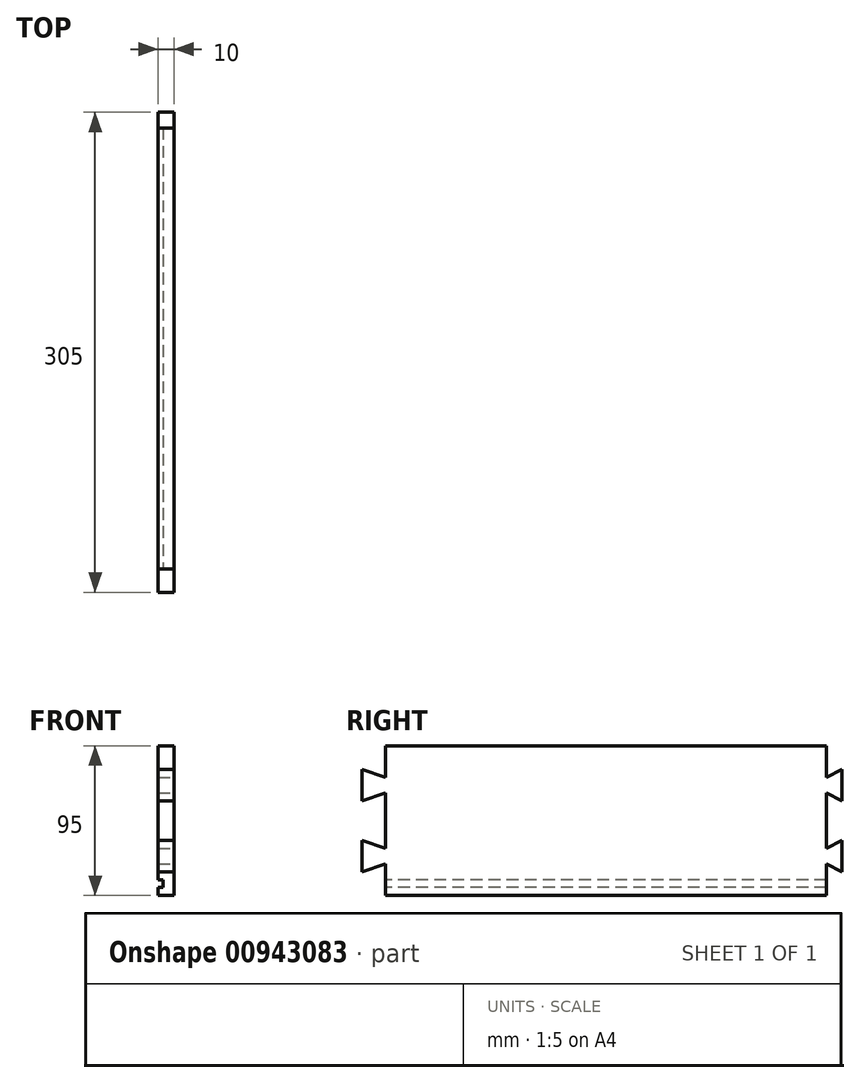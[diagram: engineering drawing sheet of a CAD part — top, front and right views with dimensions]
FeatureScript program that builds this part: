
annotation { "Feature Type Name" : "Feature", "Feature Type Description" : "" }
export const myFeature = defineFeature(function(context is Context, id is Id, definition is map)
    precondition{}
    {
        {
            var Q0;
            Q0=qCreatedBy(makeId("Right.planeOp"),FACE);
            var sketch = newSketch(context, id + "F0", { "sketchPlane" : qUnion([Q0])});
            skLineSegment(sketch, "E0.bottom", {"start": v(-82.46, 55.9) * mm, "end": v(222.54, 55.9) * mm});
            skLineSegment(sketch, "E0.top", {"start": v(-82.46, -39.1) * mm, "end": v(222.54, -39.1) * mm});
            skLineSegment(sketch, "E0.left", {"start": v(-82.46, 55.9) * mm, "end": v(-82.46, -39.1) * mm});
            skLineSegment(sketch, "E0.right", {"start": v(222.54, 55.9) * mm, "end": v(222.54, -39.1) * mm});
            skSolve(sketch);
        }
        {
            var Q0;
            Q0=makeQuery(id+"F0.imprint","IMPRINT",FACE,{"disambiguationData":[TD([[makeQuery(id+"F0.imprint","IMPRINT",EDGE,{"derivedFrom":sQuery(id+"F0.wireOp",EDGE,"E0.bottom")}),-1.0]])]});
            extrude(context, id + "F1", {"entities" : qUnion([Q0]), "depth" : 10 * mm, "offsetDistance" : 25 * mm});
        }
        {
            var Q0;
            Q0=makeQuery(id+"F1.opExtrude","CAP_FACE",FACE,{"disambiguationData":[OSD([sQuery(id+"F0.wireOp",EDGE,"E0.bottom"),sQuery(id+"F0.wireOp",EDGE,"E0.top"),sQuery(id+"F0.wireOp",EDGE,"E0.left"),sQuery(id+"F0.wireOp",EDGE,"E0.right")])],"isStart":false});
            var sketch = newSketch(context, id + "F2", { "sketchPlane" : qUnion([Q0])});
            skLineSegment(sketch, "E1", {"start": v(-82.46, 40.9) * mm, "end": v(-67.46, 35.9) * mm});
            skLineSegment(sketch, "E2", {"start": v(-67.46, 35.9) * mm, "end": v(-67.46, 55.9) * mm});
            skLineSegment(sketch, "E3", {"start": v(-67.46, 55.9) * mm, "end": v(-82.46, 55.9) * mm});
            skLineSegment(sketch, "E4", {"start": v(-82.46, 55.9) * mm, "end": v(-82.46, 40.9) * mm});
            skLineSegment(sketch, "E5", {"start": v(-82.46, -39.1) * mm, "end": v(-82.46, -24.1) * mm});
            skLineSegment(sketch, "E6", {"start": v(-82.46, -24.1) * mm, "end": v(-67.46, -19.1) * mm});
            skLineSegment(sketch, "E7", {"start": v(-67.46, -19.1) * mm, "end": v(-67.46, -39.1) * mm});
            skLineSegment(sketch, "E8", {"start": v(-67.46, -39.1) * mm, "end": v(-82.46, -39.1) * mm});
            skLineSegment(sketch, "E9", {"start": v(-82.46, 20.9) * mm, "end": v(-67.46, 25.9) * mm});
            skLineSegment(sketch, "E10", {"start": v(-67.46, 25.9) * mm, "end": v(-67.46, -9.1) * mm});
            skLineSegment(sketch, "E11", {"start": v(-67.46, -9.1) * mm, "end": v(-82.46, -4.1) * mm});
            skSolve(sketch);
        }
        {
            var Q0;
            Q0=makeQuery(id+"F2.imprint","IMPRINT",FACE,{"disambiguationData":[TD([[makeQuery(id+"F2.imprint","IMPRINT",EDGE,{"derivedFrom":sQuery(id+"F2.wireOp",EDGE,"E1")}),1.0]])]});
            var Q1;
            {var subQ0=sQuery(id+"F2.wireOp",EDGE,"E9");Q1=makeQuery(id+"F2.imprint","IMPRINT",FACE,{"disambiguationData":[TD([[makeQuery(id+"F2.imprint","IMPRINT",EDGE,{"derivedFrom":subQ0}),-1.0]])]});}
            var Q2;
            Q2=makeQuery(id+"F2.imprint","IMPRINT",FACE,{"disambiguationData":[TD([[makeQuery(id+"F2.imprint","IMPRINT",EDGE,{"derivedFrom":sQuery(id+"F2.wireOp",EDGE,"E5")}),1.0]])]});
            extrude(context, id + "F3", {"entities" : qUnion([Q0, Q1, Q2]), "operationType" : NewBodyOperationType.REMOVE, "oppositeDirection" : true, "depth" : 25 * mm, "offsetDistance" : 25 * mm});
        }
        {
            var Q0;
            Q0=makeQuery(id+"F1.opExtrude","CAP_FACE",FACE,{"disambiguationData":[OSD([sQuery(id+"F0.wireOp",EDGE,"E0.bottom"),sQuery(id+"F0.wireOp",EDGE,"E0.top"),sQuery(id+"F0.wireOp",EDGE,"E0.left"),sQuery(id+"F0.wireOp",EDGE,"E0.right")])],"isStart":true});
            var sketch = newSketch(context, id + "F4", { "sketchPlane" : qUnion([Q0])});
            skLineSegment(sketch, "E12.bottom", {"start": v(-222.54, -29.1) * mm, "end": v(67.46, -29.1) * mm});
            skLineSegment(sketch, "E12.top", {"start": v(-222.54, -34.1) * mm, "end": v(67.46, -34.1) * mm});
            skLineSegment(sketch, "E12.left", {"start": v(-222.54, -29.1) * mm, "end": v(-222.54, -34.1) * mm});
            skLineSegment(sketch, "E12.right", {"start": v(67.46, -29.1) * mm, "end": v(67.46, -34.1) * mm});
            skSolve(sketch);
        }
        {
            var Q0;
            Q0=makeQuery(id+"F4.imprint","IMPRINT",FACE,{"disambiguationData":[TD([[makeQuery(id+"F4.imprint","IMPRINT",EDGE,{"derivedFrom":sQuery(id+"F4.wireOp",EDGE,"E12.bottom")}),-1.0]])]});
            extrude(context, id + "F5", {"entities" : qUnion([Q0]), "operationType" : NewBodyOperationType.REMOVE, "oppositeDirection" : true, "depth" : 3 * mm, "offsetDistance" : 25 * mm});
        }
        {
            var Q0;
            Q0=makeQuery(id+"F1.opExtrude","CAP_FACE",FACE,{"disambiguationData":[OSD([sQuery(id+"F0.wireOp",EDGE,"E0.bottom"),sQuery(id+"F0.wireOp",EDGE,"E0.top"),sQuery(id+"F0.wireOp",EDGE,"E0.left"),sQuery(id+"F0.wireOp",EDGE,"E0.right")])],"isStart":false});
            var sketch = newSketch(context, id + "F6", { "sketchPlane" : qUnion([Q0])});
            skLineSegment(sketch, "E13", {"start": v(222.54, 40.9) * mm, "end": v(212.54, 35.9) * mm});
            skLineSegment(sketch, "E14", {"start": v(212.54, 35.9) * mm, "end": v(212.54, 55.9) * mm});
            skLineSegment(sketch, "E15", {"start": v(212.54, 55.9) * mm, "end": v(222.54, 55.9) * mm});
            skLineSegment(sketch, "E16", {"start": v(222.54, 55.9) * mm, "end": v(222.54, 20.9) * mm});
            skLineSegment(sketch, "E17", {"start": v(222.54, 20.9) * mm, "end": v(212.54, 25.9) * mm});
            skLineSegment(sketch, "E18", {"start": v(212.54, 25.9) * mm, "end": v(212.54, -9.1) * mm});
            skLineSegment(sketch, "E19", {"start": v(212.54, -9.1) * mm, "end": v(222.54, -4.1) * mm});
            skLineSegment(sketch, "E20", {"start": v(222.54, -4.1) * mm, "end": v(222.54, -24.1) * mm});
            skLineSegment(sketch, "E21", {"start": v(222.54, -24.1) * mm, "end": v(212.54, -19.1) * mm});
            skLineSegment(sketch, "E22", {"start": v(212.54, -19.1) * mm, "end": v(212.54, -39.1) * mm});
            skLineSegment(sketch, "E23", {"start": v(212.54, -39.1) * mm, "end": v(222.54, -39.1) * mm});
            skSolve(sketch);
        }
        {
            var Q0;
            {var subQ0=sQuery(id+"F6.wireOp",EDGE,"E13");Q0=makeQuery(id+"F6.imprint","IMPRINT",FACE,{"disambiguationData":[TD([[makeQuery(id+"F6.imprint","IMPRINT",EDGE,{"derivedFrom":subQ0}),-1.0]])]});}
            var Q1;
            {var subQ0=sQuery(id+"F6.wireOp",EDGE,"E17");Q1=makeQuery(id+"F6.imprint","IMPRINT",FACE,{"disambiguationData":[TD([[makeQuery(id+"F6.imprint","IMPRINT",EDGE,{"derivedFrom":subQ0}),1.0]])]});}
            var Q2;
            {var subQ0=sQuery(id+"F6.wireOp",EDGE,"E21");Q2=makeQuery(id+"F6.imprint","IMPRINT",FACE,{"disambiguationData":[TD([[makeQuery(id+"F6.imprint","IMPRINT",EDGE,{"derivedFrom":subQ0}),1.0]])]});}
            extrude(context, id + "F7", {"entities" : qUnion([Q0, Q1, Q2]), "operationType" : NewBodyOperationType.REMOVE, "oppositeDirection" : true, "depth" : 25 * mm, "offsetDistance" : 25 * mm});
        }
    });
